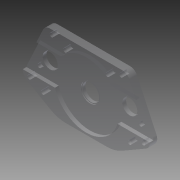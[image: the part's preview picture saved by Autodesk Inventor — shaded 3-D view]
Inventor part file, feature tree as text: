
AUTODESK INVENTOR PART (.ipt)
format: ipt  version: 2015 SP1 (Build 190203100, 203)  size: 317,952 bytes
history: native  units: in
note: dims shown in document units (in); Inventor stores cm internally (conversion verified against a paired STEP export)
features: sketch x13, projected_geometry x10, extrude x8, hole x4, reference x4, fillet x2, plane x1
ambient origin geometry x8: Origin, YZ Plane, XZ Plane, XY Plane, X Axis, Y Axis, Z Axis, Center Point
bodies: Solid1 (feature_tree)
feature tree (42):
  extrude  "Extrusion1"  Depth=8.0in
  extrude  "Extrusion2"  Depth=0.5in
  hole  "Hole1"  [1 undecoded]
  hole  "Hole2"  [1 undecoded]
  extrude  "Extrusion5"  Depth=0.5635in
  extrude  "Extrusion6"  Depth=0.5635in TaperAngle=0.0deg
  sketch  "Sketch12"  dims[d38=0.375in d39=0.0in d40=0.375in d41=0.0in]
  extrude  "Extrusion7"  Depth=0.375in TaperAngle=0.0deg
  extrude  "Extrusion9"  TaperAngle=30.0deg  [1 undecoded]
  plane  "Work Plane1"
  extrude  "Extrusion10"  Depth=2.0in
  fillet  "Fillet1"  Radius=2.0in
  hole  "Hole3"  [1 undecoded]
  extrude  "Extrusion11"  Depth=0.5in
  fillet  "Fillet2"  Radius=0.25in
  hole  "Hole4"  [1 undecoded]
  sketch  "Sketch21"  dims[d59=0.26in d60=0.75in d61=0.75in d62=0.188in d63=0.5635in d64=0.25in d65=0.8108in d66=4.375in d69=0.1718in d70=1.0in d71=0.0in d72=0.5in d73=0.25in d75=0.2905in d76=0.5in d77=3.375in d78=3.375in d79=0.5in d80=0.26in d81=0.75in d82=0.507in d83=0.25in d84=0.5635in d85=1.0in d86=0.8108in]
  sketch  "Sketch1"  dims[d0=2.5in d1=8.0in]
  sketch  "Sketch2"  dims[d2=0.5in d3=0.0in d4=0.248in]
  sketch  "Sketch7"  dims[d5=0.25in d6=0.25in d7=0.0in]
  sketch  "Sketch8"  dims[d19=0.625in d20=4.0in]
  reference  "Reference7"
  reference  "Reference8"
  reference  "Reference9"
  sketch  "Sketch10"  dims[d21=1.127in d22=0.75in d23=1.227in d24=0.06in d25=0.5635in d26=1.0in d27=0.8108in d28=1.3493in]
  sketch  "Sketch11"  dims[d29=1.0in d30=0.75in d31=0.75in d32=0.188in d33=0.5635in d34=1.0in d35=0.8108in d36=1.0in d37=0.0in]
  projected_geometry  "Projected Loop1"
  projected_geometry  "Projected Loop2"
  sketch  "Sketch15"  dims[d45=30.0deg d46=30.0deg]
  projected_geometry  "Projected Loop4"
  projected_geometry  "Projected Loop5"
  sketch  "Sketch16"  dims[d47=2.0in d48=2.3in d49=2.0in]
  projected_geometry  "Projected Loop6"
  sketch  "Sketch18"  dims[d50=0.5in d51=0.0in d52=4.35in]
  reference  "Reference11"
  sketch  "Sketch19"  dims[d53=0.25in d54=0.0in d55=0.5in d56=0.25in]
  sketch  "Sketch20"  dims[d58=0.2905in]
  projected_geometry  "Projected Loop7"
  projected_geometry  "Projected Loop8"
  projected_geometry  "Projected Loop9"
  projected_geometry  "Projected Loop10"
  projected_geometry  "Projected Loop11"
note: 5 required parameter values undecoded (feature->parameter linkage not recoverable at this tier; creation-order binding heuristic only, values carry confidence <= 0.55)
